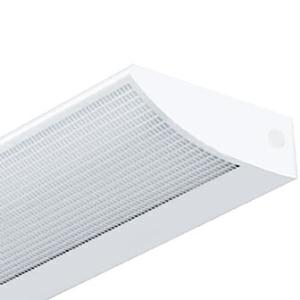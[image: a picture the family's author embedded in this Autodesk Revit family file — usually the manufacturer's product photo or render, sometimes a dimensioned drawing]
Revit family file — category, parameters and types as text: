
# Revit family: 3f_filippi_-_mira_par_dec_3f_filippi_-_1963_-_mira_par_led_de_4x12w_dali_l675
name_source: partatom
category: Lighting Fixtures
units: mm (PartAtom-declared; Revit-internal decimal feet)

## family parameters
Cut with Voids When Loaded = No
Host = Face
Light Source = No
Part Type = Normal
Room Calculation Point = No
Round Connector Dimension = Use Diameter
Shared = No

## types (1)
- 3F Filippi - Mira Par Dec (1 x LED, 6699 lm, 54 W, 4000 K)
    Apparent Load = 54 VA
    Approval mark = ENEC
    CIE Flux Codes = 42 71 90 4 100
    Color Rendering = 80
    Color Temperature = 4000 K
    Control Gear = Electronic transformer
    Default Elevation = 1800 mm
    Description = ILLUMINOTECHNICAL
Luminous efficiency 100% (DLOR 4%, ULOR 96%).
Initial luminous flux of the luminaire 6699 lm.
Asymmetric direct-indirect distribution.
Average luminance <1000 cd/m² for radial angles >65°.
Beam angle: 108° - 110°.
Luminous efficacy 124 lm/W.
Lifetime (L93/B10): 30000 h. (tq+25°C)
Lifetime (L90/B10): 50000 h. (tq+25°C)
Lifetime (L85/B10): 80000 h. (tq+25°C)
Lifetime (L80/B10): 100000 h. (tq+25°C)
Sudden decreased luminous flux after 50000 hours: 0% (C0).
Photobiological safety in compliance with IEC/TR 62778: RG0 risk exempt, (IEC 62471).
In compliance with IEC/EN 62722-2-1 - IEC/EN 62717 standards.

SOURCE
4 linear LED modules 12W/840.
Energy efficiency class (UE 2019/2020 - UE 2019/2015): D.
CIE 13.3 Colour rendering index: CRI >80 (R9 <50%).
IES TM-30 Fidelity Index: Rf = 84 Rg = 95.
CCT nominal colour temperature 4000 K.
Colour initial tolerance (MacAdam): SDCM 3.

MECHANICAL
Housing in galvannealed steel, painted in white epoxy-polyester with reticular slots for high direct light emission.
Opal polycarbonate shielding film over the lower reticular zone.
Asymmetric flow recuperator, high efficiency, in specular aluminium with superficial titanium-magnesium treatment.
Opal acrylic upper diffuser.
Luminaire with limited surface temperature. - D - (EN 60598-2-24)
Dimensions: 675x230 mm, height 80 mm. Weight 2.665 kg.
IP40 protection degree.
Glow-wire test resistance 650°C.

ELECTRICAL
Halogen Free DALI-2, PUSH-DIM, electronic wiring 230V-50/60Hz, power factor 0.95 at full load, THD <25%, constant output current, SELV, class I, 1 driver, 1 DALI addresse.
Power of the luminaire 54 W.
CE - IEC 60598-1 - EN 60598-1.
SAFE FLICKER: PstLM=<1 and SVM=<0.4 (IEC TR 61547-1 and IEC TR 63158), to ensure a more comfortable and safe light.
Luminaire compliant with EN 60598-2-22 for power supply from a centralised emergency system CPSS (Central Power Supply System), not incorporated in the luminaire - high risk areas excluded. The default power and flux are 100% in AC and 15% in DC.
Ambient temperature from 0°C to +25°C.
Temperature class T6 max 85°C.
Relative humidity UR: <85%.

INSTALLATION
Wall.
All accessories dedicated to this product are available on the Catalog and on our website www.3F-Filippi.com.

APPLICATIONS
Environments where a comfortable light is required. Luminaire for wall mounting, with an essential and modern design. Suitable for offices, conference rooms, managerial offices.

LIGHT MANAGEMENT
Recommended minimum setting: 10%.
The device, equipped with DALI-2 driver, can be controlled manually with 3F Easy Dim technology or automatically/manually with 3F Smart Dimming technology and/or centralised DALI systems.
DALI-2 certification guarantees interoperability with other devices with the same certification.
In electrical systems without a regulation system (manual or automatic) and DALI bus, a suitable jumper must be made on the DA-DA terminals of the appliance.

WARNING
Luminaire designed for disposal/recycling at end-of-life.
Replaceable (LED only) light source by a professional. Replaceable control gear by a professional.
    Height = 80 mm  [stored 0.262467 ft]
    Lamp = 1 x LED
    Lamp Light Flux = 6699 lm
    Lamp Power = 54 W
    Lamp count = 1
    Length = 675 mm
    Lifetime = 50000 h
    Luminous efficacy = 124 lm/W
    Manufacturer = 3F Filippi
    ModVariant = No
    Model = 3F Filippi - 1963 - Mira Par LED DE 4x12W DALI L675
    Mounting Place = Wall
    Mounting Type = Surface mounted
    Number of Poles = 1
    OnlyDefault = Yes
    Power Factor = 1
    Product Name = 3F Filippi - Mira Par Dec
    Product group = wall-mounted luminaire
    ProductGroupID = 20
    Protection Class = Protection class I
    Protection Degree = IP 40
    RLX_Detail_Level = 1
    RLX_Emergency_Light_Flux = 0 lm
    RLX_Emergency_Type = 0
    RLX_Emergency_Type_DB = No
    RlxData = <blob elided: 61373 chars, md5=be954624>
    Socket = socket
    Standby Power = 0 W
    System Light Flux = 6699 lm
    System Power = 54 W
    Type Comments = Product without accessories
    Type Image = 3ffilippi_mira_par.jpg
    URL = http://relux.com
    VarID = ---
    Voltage = 0 V
    Weight = 0.00 kg
    Width = 230 mm

note: [stored X ft] marks values corroborated as IEEE doubles in the binary element streams (Revit-internal decimal feet)

## geometry (parser evidence)
native form markers: Blend x4, Sweep x12
no freeform markers — native parametric forms only
